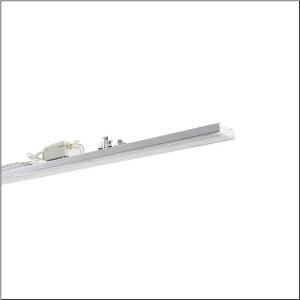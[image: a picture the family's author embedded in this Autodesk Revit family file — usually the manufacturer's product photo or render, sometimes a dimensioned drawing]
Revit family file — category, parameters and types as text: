
# Revit family: licross_11_recessed_mo_51tl10mn4axg
name_source: partatom
category: Lighting Fixtures
units: mm (PartAtom-declared; Revit-internal decimal feet)

## family parameters
Cut with Voids When Loaded = No
Host = Face
Light Source = No
Part Type = Normal
Room Calculation Point = No
Round Connector Dimension = Use Diameter
Shared = No

## types (1)
- --- (1 x LED, 10000 lm, 55.2 W, 4000K)
    Apparent Load = 55 VA
    CIE Flux Codes = 50 81 96 100 100
    Color Rendering = 80
    Color Temperature = 4000K
    Default Elevation = 1800 mm
    Description = Licross 11 Recessed MO, luminaire insert, of sheet steel, coil coated, white, length: 1.500mm, width: 66mm, height: 67mm, LED rated luminous flux: 10.000lm, light colour: 840, SDCM (Standard Deviation of Colour Matching)MacAdam ≤ 2 SDCM (initial), control gear: ON/OFF Multilumen, with plug, 3-pole, with phase selection, mains connection: 220..240V, AC, 50/60Hz, rated input power: 55W, internal wiring halogen-free, primary optical cover: cover, of PMMA, light emission: direct distribution, primary light characteristic: symmetric, protection rating (complete): IP40, insulation class (complete): insulation class I (protective earthing), certification: CE, ENEC, VDE, UKCA, protection symbol: D if used in an environment without relevant dust loads with corresponding accessories, impact resistance: IK06, permissible ambient temperature for indoor applications: -35..+40°C, corresponds to IFS (International Featured Standards) requirements for safety and quality in the food industry, reducing of maximum allowable ambient temperature of 5°C with ceiling mounting, The light source and the operating device comply with the requirements of the Ecodesign Regulation (EU) 2019/2020 and are replaceable in accordance with this regulation, packaging unit: 1 piece
    Height = 58 mm
    Lamp = 1 x LED
    Lamp Light Flux = 10000 lm
    Lamp Power = 55.2 W
    Lamp count = 1
    Length = 1500 mm
    Luminous efficacy = 181 lm/W
    Manufacturer = Siteco
    ModVariant = No
    Model = 51TL10MN4AXG
    Mounting Place = Ceiling
    Mounting Type = Pendant
    Number of Poles = 1
    OnlyDefault = Yes
    Power Factor = 1
    Product Name = Licross 11 Recessed MO
    Product group = luminaire insert | ceiling pendant
    ProductGroupID = 901
    Protection Class = Protection class I
    Protection Degree = IP 40
    RLX_Detail_Level = 1
    RLX_Emergency_Light_Flux = 0 lm
    RLX_Emergency_Type = 0
    RLX_Emergency_Type_DB = No
    RlxData = <blob elided: 22353 chars, md5=6426a76d>
    Socket = socket
    Standby Power = 0 W
    System Light Flux = 10000 lm
    System Power = 55 W
    Type Comments = factory setting: luminous flux: 100 % | (A | C | E) | 126 mA
    Type Image = l_1296930.jpg
    URL = http://relux.com
    VarID = @adj_091519
    Voltage = 0 V
    Weight = 0.00 kg
    Width = 66 mm

## geometry (parser evidence)
native form markers: Blend x4, Sweep x10
no freeform markers — native parametric forms only
